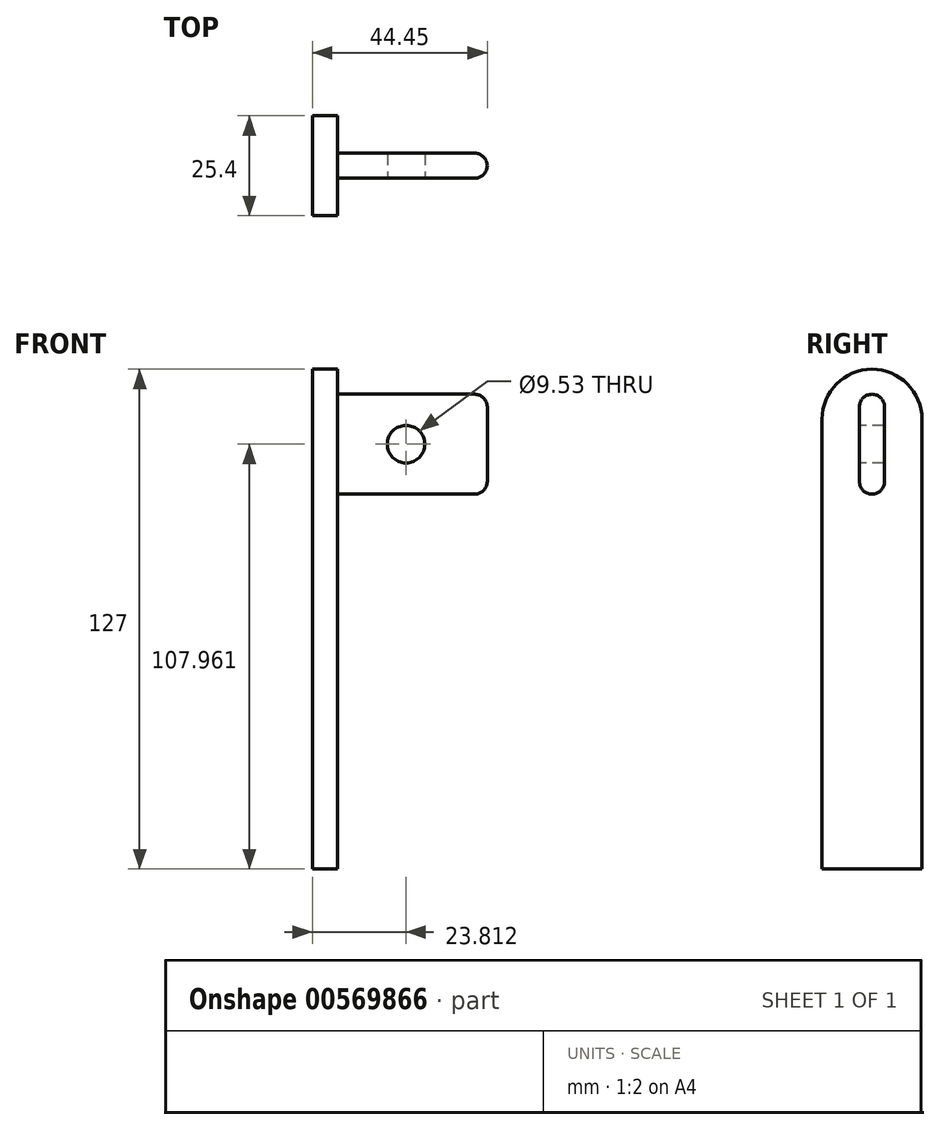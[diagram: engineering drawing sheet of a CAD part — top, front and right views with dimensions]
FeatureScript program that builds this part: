
annotation { "Feature Type Name" : "Feature", "Feature Type Description" : "" }
export const myFeature = defineFeature(function(context is Context, id is Id, definition is map)
    precondition{}
    {
        {
            var Q0;
            Q0=qCreatedBy(makeId("Front.planeOp"),FACE);
            var sketch = newSketch(context, id + "F0", { "sketchPlane" : qUnion([Q0])});
            skLineSegment(sketch, "E0.bottom", {"start": v(0, 0) * mm, "end": v(6.35, 0) * mm});
            skLineSegment(sketch, "E0.top", {"start": v(0, 127) * mm, "end": v(6.35, 127) * mm});
            skLineSegment(sketch, "E0.left", {"start": v(0, 0) * mm, "end": v(0, 127) * mm});
            skLineSegment(sketch, "E0.right", {"start": v(6.35, 0) * mm, "end": v(6.35, 127) * mm});
            skSolve(sketch);
        }
        {
            var Q0;
            Q0 = qSketchRegion(id + "F0", true);
            extrude(context, id + "F1", {"entities" : qUnion([Q0]), "depth" : 25.4 * mm, "offsetDistance" : 25.4 * mm});
        }
        {
            var Q0;
            Q0=makeQuery(id+"F1.opExtrude","CAP_EDGE",EDGE,{"disambiguationData":[OSD([sQuery(id+"F0.wireOp",EDGE,"E0.top")])],"isStart":false});
            var Q1;
            Q1=makeQuery(id+"F1.opExtrude","CAP_EDGE",EDGE,{"disambiguationData":[OSD([sQuery(id+"F0.wireOp",EDGE,"E0.top")])],"isStart":true});
            fillet(context, id + "F2", {"entities" : qUnion([Q0, Q1]), "radius" : 12.7 * mm, "tangentPropagation" : true, "allowEdgeOverflow" : false});
        }
        {
            var Q0;
            Q0=makeQuery(id+"F1.opExtrude","SWEPT_FACE",FACE,{"disambiguationData":[OSD([sQuery(id+"F0.wireOp",EDGE,"E0.right")])]});
            var sketch = newSketch(context, id + "F3", { "sketchPlane" : qUnion([Q0])});
            skLineSegment(sketch, "E1.bottom", {"start": v(-15.88, 120.65) * mm, "end": v(-9.53, 120.65) * mm});
            skLineSegment(sketch, "E1.top", {"start": v(-15.88, 95.27) * mm, "end": v(-9.53, 95.27) * mm});
            skLineSegment(sketch, "E1.left", {"start": v(-15.88, 120.65) * mm, "end": v(-15.88, 95.27) * mm});
            skLineSegment(sketch, "E1.right", {"start": v(-9.53, 120.65) * mm, "end": v(-9.52, 95.27) * mm});
            skSolve(sketch);
        }
        {
            var Q0;
            Q0 = qSketchRegion(id + "F3", true);
            extrude(context, id + "F4", {"entities" : qUnion([Q0]), "operationType" : NewBodyOperationType.ADD, "depth" : 38.1 * mm, "offsetDistance" : 25.4 * mm});
        }
        {
            var Q0;
            Q0=makeQuery(id+"F4.opExtrude","SWEPT_EDGE",EDGE,{"disambiguationData":[OSD([sQuery(id+"F3.wireOp",EDGE,"E1.bottom"),sQuery(id+"F3.wireOp",EDGE,"E1.left")])]});
            var Q1;
            Q1=makeQuery(id+"F4.opExtrude","SWEPT_EDGE",EDGE,{"disambiguationData":[OSD([sQuery(id+"F3.wireOp",EDGE,"E1.bottom"),sQuery(id+"F3.wireOp",EDGE,"E1.right")])]});
            var Q2;
            Q2=makeQuery(id+"F4.opExtrude","SWEPT_EDGE",EDGE,{"disambiguationData":[OSD([sQuery(id+"F3.wireOp",EDGE,"E1.top"),sQuery(id+"F3.wireOp",EDGE,"E1.left")])]});
            var Q3;
            Q3=makeQuery(id+"F4.opExtrude","SWEPT_EDGE",EDGE,{"disambiguationData":[OSD([sQuery(id+"F3.wireOp",EDGE,"E1.top"),sQuery(id+"F3.wireOp",EDGE,"E1.right")])]});
            var Q4;
            Q4=makeQuery(id+"F4.opExtrude","CAP_EDGE",EDGE,{"disambiguationData":[OSD([sQuery(id+"F3.wireOp",EDGE,"E1.left")])],"isStart":false});
            var Q5;
            Q5=makeQuery(id+"F4.opExtrude","CAP_EDGE",EDGE,{"disambiguationData":[OSD([sQuery(id+"F3.wireOp",EDGE,"E1.right")])],"isStart":false});
            var Q6;
            Q6=makeQuery(id+"F4.opExtrude","CAP_EDGE",EDGE,{"disambiguationData":[OSD([sQuery(id+"F3.wireOp",EDGE,"E1.top")])],"isStart":false});
            var Q7;
            Q7=makeQuery(id+"F4.opExtrude","CAP_EDGE",EDGE,{"disambiguationData":[OSD([sQuery(id+"F3.wireOp",EDGE,"E1.bottom")])],"isStart":false});
            fillet(context, id + "F5", {"entities" : qUnion([Q0, Q1, Q2, Q3, Q4, Q5, Q6, Q7]), "radius" : 3.17 * mm, "tangentPropagation" : true, "allowEdgeOverflow" : false});
        }
        {
            var Q0;
            Q0=makeQuery(id+"F4.opExtrude","SWEPT_FACE",FACE,{"disambiguationData":[OSD([sQuery(id+"F3.wireOp",EDGE,"E1.left")])]});
            var sketch = newSketch(context, id + "F6", { "sketchPlane" : qUnion([Q0])});
            skCircle(sketch, "E2", {"center": v(23.81, 107.96) * mm, "radius": 4.76 * mm});
            skPoint(sketch, "E2.centerSnap0", {"position": v(23.81, 98.45) * mm});
            skPoint(sketch, "E2.centerSnap1", {"position": v(6.35, 107.96) * mm});
            skSolve(sketch);
        }
        {
            var Q0;
            Q0 = qSketchRegion(id + "F6", true);
            extrude(context, id + "F7", {"entities" : qUnion([Q0]), "operationType" : NewBodyOperationType.REMOVE, "oppositeDirection" : true, "depth" : 25.4 * mm, "offsetDistance" : 25.4 * mm});
        }
    });
